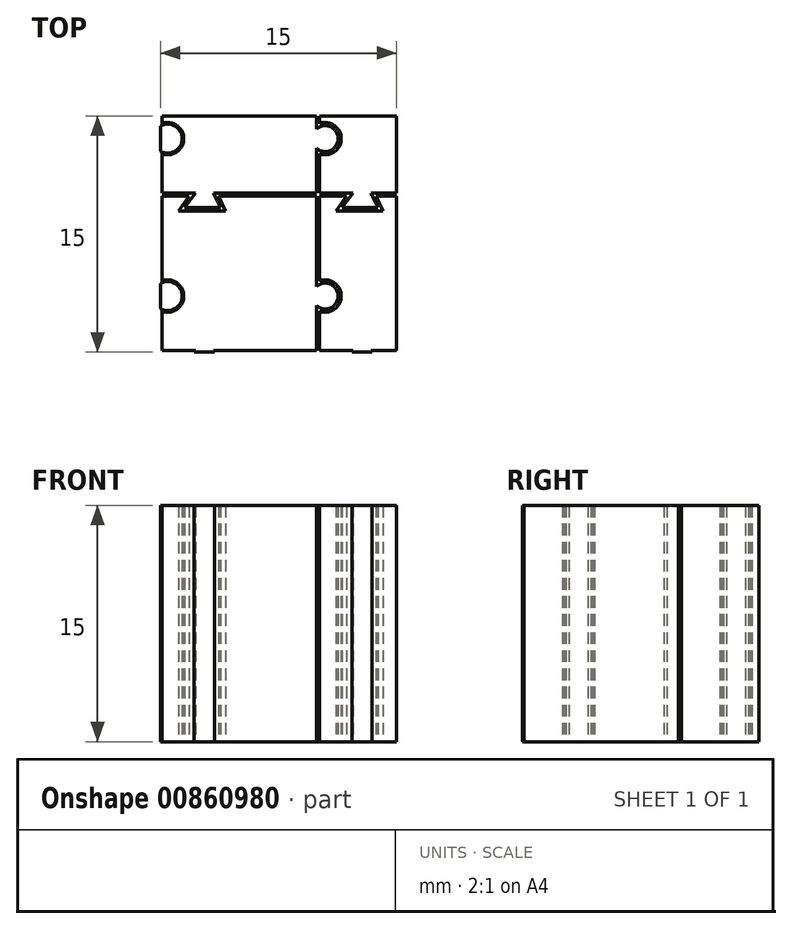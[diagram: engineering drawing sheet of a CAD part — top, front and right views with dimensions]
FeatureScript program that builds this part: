
annotation { "Feature Type Name" : "Feature", "Feature Type Description" : "" }
export const myFeature = defineFeature(function(context is Context, id is Id, definition is map)
    precondition{}
    {
        {
            var Q0;
            Q0=qCreatedBy(makeId("Top.planeOp"),FACE);
            var sketch = newSketch(context, id + "F0", { "sketchPlane" : qUnion([Q0])});
            skLineSegment(sketch, "E0.bottom", {"start": v(0, 0) * mm, "end": v(2.03, 0) * mm});
            skLineSegment(sketch, "E0.top", {"start": v(0, 10) * mm, "end": v(2.03, 10) * mm});
            skLineSegment(sketch, "E0.left", {"start": v(0, 0) * mm, "end": v(0, 2.75) * mm});
            skLineSegment(sketch, "E0.right", {"start": v(10, 0) * mm, "end": v(10, 2.75) * mm});
            skLineSegment(sketch, "E1", {"start": v(2.03, 10) * mm, "end": v(1.34, 9.07) * mm});
            skLineSegment(sketch, "E2", {"start": v(1.34, 9.07) * mm, "end": v(3.97, 9.07) * mm});
            skLineSegment(sketch, "E3", {"start": v(3.97, 9.07) * mm, "end": v(3.54, 10) * mm});
            skLineSegment(sketch, "E4.trimOffspring", {"start": v(3.54, 10) * mm, "end": v(10, 10) * mm});
            skLineSegment(sketch, "E5", {"start": v(2.03, 0) * mm, "end": v(1.34, -0.93) * mm});
            skLineSegment(sketch, "E6", {"start": v(1.34, -0.93) * mm, "end": v(3.97, -0.93) * mm});
            skLineSegment(sketch, "E7", {"start": v(3.97, -0.93) * mm, "end": v(3.54, 0) * mm});
            skLineSegment(sketch, "E8.trimOffspring", {"start": v(3.54, 0) * mm, "end": v(10, 0) * mm});
            skArc(sketch, "E9", {"start": v(0, 2.75) * mm, "mid": v(1.38, 3.55) * mm, "end": v(0, 4.36) * mm});
            skLineSegment(sketch, "E10.trimOffspring", {"start": v(0, 4.36) * mm, "end": v(0, 10) * mm});
            skArc(sketch, "E11", {"start": v(10, 2.75) * mm, "mid": v(11.38, 3.55) * mm, "end": v(10, 4.36) * mm});
            skLineSegment(sketch, "E12.trimOffspring", {"start": v(10, 4.36) * mm, "end": v(10, 10) * mm});
            skArc(sketch, "E13.0", {"start": v(0.1, 2.6) * mm, "mid": v(1.48, 3.55) * mm, "end": v(0.1, 4.51) * mm});
            skLineSegment(sketch, "E13.1", {"start": v(0.1, 0.1) * mm, "end": v(0.1, 2.6) * mm});
            skLineSegment(sketch, "E13.2", {"start": v(0.1, 0.1) * mm, "end": v(2.23, 0.1) * mm});
            skLineSegment(sketch, "E13.3", {"start": v(2.23, 0.1) * mm, "end": v(1.54, -0.83) * mm});
            skLineSegment(sketch, "E13.4", {"start": v(1.54, -0.83) * mm, "end": v(3.81, -0.83) * mm});
            skLineSegment(sketch, "E13.5", {"start": v(4.13, 8.97) * mm, "end": v(3.7, 9.9) * mm});
            skLineSegment(sketch, "E13.6", {"start": v(1.14, 8.97) * mm, "end": v(4.13, 8.97) * mm});
            skLineSegment(sketch, "E13.7", {"start": v(1.83, 9.9) * mm, "end": v(1.14, 8.97) * mm});
            skLineSegment(sketch, "E13.8", {"start": v(0.1, 9.9) * mm, "end": v(1.83, 9.9) * mm});
            skLineSegment(sketch, "E13.9", {"start": v(3.7, 9.9) * mm, "end": v(9.9, 9.9) * mm});
            skLineSegment(sketch, "E13.10", {"start": v(9.9, 4.16) * mm, "end": v(9.9, 9.9) * mm});
            skArc(sketch, "E13.11", {"start": v(9.9, 2.95) * mm, "mid": v(11.28, 3.55) * mm, "end": v(9.9, 4.16) * mm});
            skLineSegment(sketch, "E13.12", {"start": v(9.9, 0.1) * mm, "end": v(9.9, 2.95) * mm});
            skLineSegment(sketch, "E13.13", {"start": v(3.39, 0.1) * mm, "end": v(9.9, 0.1) * mm});
            skLineSegment(sketch, "E13.14", {"start": v(0.1, 4.51) * mm, "end": v(0.1, 9.9) * mm});
            skLineSegment(sketch, "E13.15", {"start": v(3.81, -0.83) * mm, "end": v(3.39, 0.1) * mm});
            skLineSegment(sketch, "E14.0.1.0", {"start": v(1.14, 18.97) * mm, "end": v(4.13, 18.97) * mm});
            skLineSegment(sketch, "E14.0.1.1", {"start": v(0.1, 19.9) * mm, "end": v(1.83, 19.9) * mm});
            skArc(sketch, "E14.0.1.3", {"start": v(10, 12.75) * mm, "mid": v(11.38, 13.55) * mm, "end": v(10, 14.36) * mm});
            skArc(sketch, "E14.0.1.4", {"start": v(9.9, 12.95) * mm, "mid": v(11.28, 13.55) * mm, "end": v(9.9, 14.16) * mm});
            skArc(sketch, "E14.0.1.5", {"start": v(0, 12.75) * mm, "mid": v(1.38, 13.55) * mm, "end": v(0, 14.36) * mm});
            skLineSegment(sketch, "E14.0.1.6", {"start": v(10, 10) * mm, "end": v(10, 12.75) * mm});
            skArc(sketch, "E14.0.1.7", {"start": v(0.1, 12.6) * mm, "mid": v(1.48, 13.55) * mm, "end": v(0.1, 14.51) * mm});
            skLineSegment(sketch, "E14.0.1.8", {"start": v(0.1, 10.1) * mm, "end": v(2.23, 10.1) * mm});
            skLineSegment(sketch, "E14.0.1.10", {"start": v(9.9, 10.1) * mm, "end": v(9.9, 12.95) * mm});
            skLineSegment(sketch, "E14.0.1.11", {"start": v(10, 14.36) * mm, "end": v(10, 20) * mm});
            skLineSegment(sketch, "E14.0.1.12", {"start": v(0, 20) * mm, "end": v(2.03, 20) * mm});
            skLineSegment(sketch, "E14.0.1.13", {"start": v(3.7, 19.9) * mm, "end": v(9.9, 19.9) * mm});
            skLineSegment(sketch, "E14.0.1.14", {"start": v(0, 14.36) * mm, "end": v(0, 20) * mm});
            skLineSegment(sketch, "E14.0.1.15", {"start": v(9.9, 14.16) * mm, "end": v(9.9, 19.9) * mm});
            skLineSegment(sketch, "E14.0.1.16", {"start": v(3.54, 20) * mm, "end": v(10, 20) * mm});
            skLineSegment(sketch, "E14.0.1.17", {"start": v(0.1, 10.1) * mm, "end": v(0.1, 12.6) * mm});
            skLineSegment(sketch, "E14.0.1.18", {"start": v(1.34, 19.07) * mm, "end": v(3.97, 19.07) * mm});
            skLineSegment(sketch, "E14.0.1.19", {"start": v(1.54, 9.17) * mm, "end": v(3.81, 9.17) * mm});
            skLineSegment(sketch, "E14.0.1.21", {"start": v(0.1, 14.51) * mm, "end": v(0.1, 19.9) * mm});
            skLineSegment(sketch, "E14.0.1.22", {"start": v(0, 10) * mm, "end": v(0, 12.75) * mm});
            skLineSegment(sketch, "E14.0.1.23", {"start": v(3.39, 10.1) * mm, "end": v(9.9, 10.1) * mm});
            skLineSegment(sketch, "E14.0.1.24", {"start": v(2.03, 20) * mm, "end": v(1.34, 19.07) * mm});
            skLineSegment(sketch, "E14.0.1.26", {"start": v(4.13, 18.97) * mm, "end": v(3.7, 19.9) * mm});
            skLineSegment(sketch, "E14.0.1.28", {"start": v(3.81, 9.17) * mm, "end": v(3.39, 10.1) * mm});
            skLineSegment(sketch, "E14.0.1.29", {"start": v(3.97, 19.07) * mm, "end": v(3.54, 20) * mm});
            skLineSegment(sketch, "E14.0.1.30", {"start": v(1.83, 19.9) * mm, "end": v(1.14, 18.97) * mm});
            skLineSegment(sketch, "E14.0.1.31", {"start": v(2.23, 10.1) * mm, "end": v(1.54, 9.17) * mm});
            skLineSegment(sketch, "E14.1.0.0", {"start": v(11.14, 8.97) * mm, "end": v(14.13, 8.97) * mm});
            skLineSegment(sketch, "E14.1.0.1", {"start": v(10.1, 9.9) * mm, "end": v(11.83, 9.9) * mm});
            skLineSegment(sketch, "E14.1.0.2", {"start": v(11.34, -0.93) * mm, "end": v(13.97, -0.93) * mm});
            skArc(sketch, "E14.1.0.3", {"start": v(20, 2.75) * mm, "mid": v(21.38, 3.55) * mm, "end": v(20, 4.36) * mm});
            skArc(sketch, "E14.1.0.4", {"start": v(19.9, 2.95) * mm, "mid": v(21.28, 3.55) * mm, "end": v(19.9, 4.16) * mm});
            skLineSegment(sketch, "E14.1.0.6", {"start": v(20, 0) * mm, "end": v(20, 2.75) * mm});
            skArc(sketch, "E14.1.0.7", {"start": v(10.1, 2.6) * mm, "mid": v(11.48, 3.55) * mm, "end": v(10.1, 4.51) * mm});
            skLineSegment(sketch, "E14.1.0.8", {"start": v(10.1, 0.1) * mm, "end": v(12.23, 0.1) * mm});
            skLineSegment(sketch, "E14.1.0.9", {"start": v(13.54, 0) * mm, "end": v(20, 0) * mm});
            skLineSegment(sketch, "E14.1.0.10", {"start": v(19.9, 0.1) * mm, "end": v(19.9, 2.95) * mm});
            skLineSegment(sketch, "E14.1.0.11", {"start": v(20, 4.36) * mm, "end": v(20, 10) * mm});
            skLineSegment(sketch, "E14.1.0.12", {"start": v(10, 10) * mm, "end": v(12.03, 10) * mm});
            skLineSegment(sketch, "E14.1.0.13", {"start": v(13.7, 9.9) * mm, "end": v(19.9, 9.9) * mm});
            skLineSegment(sketch, "E14.1.0.15", {"start": v(19.9, 4.16) * mm, "end": v(19.9, 9.9) * mm});
            skLineSegment(sketch, "E14.1.0.16", {"start": v(13.54, 10) * mm, "end": v(20, 10) * mm});
            skLineSegment(sketch, "E14.1.0.17", {"start": v(10.1, 0.1) * mm, "end": v(10.1, 2.6) * mm});
            skLineSegment(sketch, "E14.1.0.18", {"start": v(11.34, 9.07) * mm, "end": v(13.97, 9.07) * mm});
            skLineSegment(sketch, "E14.1.0.19", {"start": v(11.54, -0.83) * mm, "end": v(13.81, -0.83) * mm});
            skLineSegment(sketch, "E14.1.0.20", {"start": v(10, 0) * mm, "end": v(12.03, 0) * mm});
            skLineSegment(sketch, "E14.1.0.21", {"start": v(10.1, 4.51) * mm, "end": v(10.1, 9.9) * mm});
            skLineSegment(sketch, "E14.1.0.23", {"start": v(13.39, 0.1) * mm, "end": v(19.9, 0.1) * mm});
            skLineSegment(sketch, "E14.1.0.24", {"start": v(12.03, 10) * mm, "end": v(11.34, 9.07) * mm});
            skLineSegment(sketch, "E14.1.0.25", {"start": v(13.97, -0.93) * mm, "end": v(13.54, 0) * mm});
            skLineSegment(sketch, "E14.1.0.26", {"start": v(14.13, 8.97) * mm, "end": v(13.7, 9.9) * mm});
            skLineSegment(sketch, "E14.1.0.27", {"start": v(12.03, 0) * mm, "end": v(11.34, -0.93) * mm});
            skLineSegment(sketch, "E14.1.0.28", {"start": v(13.81, -0.83) * mm, "end": v(13.39, 0.1) * mm});
            skLineSegment(sketch, "E14.1.0.29", {"start": v(13.97, 9.07) * mm, "end": v(13.54, 10) * mm});
            skLineSegment(sketch, "E14.1.0.30", {"start": v(11.83, 9.9) * mm, "end": v(11.14, 8.97) * mm});
            skLineSegment(sketch, "E14.1.0.31", {"start": v(12.23, 0.1) * mm, "end": v(11.54, -0.83) * mm});
            skLineSegment(sketch, "E14.1.1.0", {"start": v(11.14, 18.97) * mm, "end": v(14.13, 18.97) * mm});
            skLineSegment(sketch, "E14.1.1.1", {"start": v(10.1, 19.9) * mm, "end": v(11.83, 19.9) * mm});
            skLineSegment(sketch, "E14.1.1.2", {"start": v(11.34, 9.07) * mm, "end": v(13.97, 9.07) * mm});
            skArc(sketch, "E14.1.1.3", {"start": v(20, 12.75) * mm, "mid": v(21.38, 13.55) * mm, "end": v(20, 14.36) * mm});
            skArc(sketch, "E14.1.1.4", {"start": v(19.9, 12.95) * mm, "mid": v(21.28, 13.55) * mm, "end": v(19.9, 14.16) * mm});
            skArc(sketch, "E14.1.1.5", {"start": v(10, 12.75) * mm, "mid": v(11.38, 13.55) * mm, "end": v(10, 14.36) * mm});
            skLineSegment(sketch, "E14.1.1.6", {"start": v(20, 10) * mm, "end": v(20, 12.75) * mm});
            skArc(sketch, "E14.1.1.7", {"start": v(10.1, 12.6) * mm, "mid": v(11.48, 13.55) * mm, "end": v(10.1, 14.51) * mm});
            skLineSegment(sketch, "E14.1.1.8", {"start": v(10.1, 10.1) * mm, "end": v(12.23, 10.1) * mm});
            skLineSegment(sketch, "E14.1.1.9", {"start": v(13.54, 10) * mm, "end": v(20, 10) * mm});
            skLineSegment(sketch, "E14.1.1.10", {"start": v(19.9, 10.1) * mm, "end": v(19.9, 12.95) * mm});
            skLineSegment(sketch, "E14.1.1.11", {"start": v(20, 14.36) * mm, "end": v(20, 20) * mm});
            skLineSegment(sketch, "E14.1.1.12", {"start": v(10, 20) * mm, "end": v(12.03, 20) * mm});
            skLineSegment(sketch, "E14.1.1.13", {"start": v(13.7, 19.9) * mm, "end": v(19.9, 19.9) * mm});
            skLineSegment(sketch, "E14.1.1.14", {"start": v(10, 14.36) * mm, "end": v(10, 20) * mm});
            skLineSegment(sketch, "E14.1.1.15", {"start": v(19.9, 14.16) * mm, "end": v(19.9, 19.9) * mm});
            skLineSegment(sketch, "E14.1.1.16", {"start": v(13.54, 20) * mm, "end": v(20, 20) * mm});
            skLineSegment(sketch, "E14.1.1.17", {"start": v(10.1, 10.1) * mm, "end": v(10.1, 12.6) * mm});
            skLineSegment(sketch, "E14.1.1.18", {"start": v(11.34, 19.07) * mm, "end": v(13.97, 19.07) * mm});
            skLineSegment(sketch, "E14.1.1.19", {"start": v(11.54, 9.17) * mm, "end": v(13.81, 9.17) * mm});
            skLineSegment(sketch, "E14.1.1.20", {"start": v(10, 10) * mm, "end": v(12.03, 10) * mm});
            skLineSegment(sketch, "E14.1.1.21", {"start": v(10.1, 14.51) * mm, "end": v(10.1, 19.9) * mm});
            skLineSegment(sketch, "E14.1.1.22", {"start": v(10, 10) * mm, "end": v(10, 12.75) * mm});
            skLineSegment(sketch, "E14.1.1.23", {"start": v(13.39, 10.1) * mm, "end": v(19.9, 10.1) * mm});
            skLineSegment(sketch, "E14.1.1.24", {"start": v(12.03, 20) * mm, "end": v(11.34, 19.07) * mm});
            skLineSegment(sketch, "E14.1.1.25", {"start": v(13.97, 9.07) * mm, "end": v(13.54, 10) * mm});
            skLineSegment(sketch, "E14.1.1.26", {"start": v(14.13, 18.97) * mm, "end": v(13.7, 19.9) * mm});
            skLineSegment(sketch, "E14.1.1.27", {"start": v(12.03, 10) * mm, "end": v(11.34, 9.07) * mm});
            skLineSegment(sketch, "E14.1.1.28", {"start": v(13.81, 9.17) * mm, "end": v(13.39, 10.1) * mm});
            skLineSegment(sketch, "E14.1.1.29", {"start": v(13.97, 19.07) * mm, "end": v(13.54, 20) * mm});
            skLineSegment(sketch, "E14.1.1.30", {"start": v(11.83, 19.9) * mm, "end": v(11.14, 18.97) * mm});
            skLineSegment(sketch, "E14.1.1.31", {"start": v(12.23, 10.1) * mm, "end": v(11.54, 9.17) * mm});
            skLineSegment(sketch, "E14.direction1", {"start": v(0, 0) * mm, "end": v(10, 0) * mm, "construction": true});
            skLineSegment(sketch, "E14.direction2", {"start": v(0, 0) * mm, "end": v(0, 10) * mm, "construction": true});
            skSolve(sketch);
        }
        {
            var Q0;
            Q0=qCreatedBy(makeId("Top.planeOp"),FACE);
            var sketch = newSketch(context, id + "F1", { "sketchPlane" : qUnion([Q0])});
            skLineSegment(sketch, "E15.bottom", {"start": v(0, 0) * mm, "end": v(15, 0) * mm});
            skLineSegment(sketch, "E15.top", {"start": v(0, 15) * mm, "end": v(15, 15) * mm});
            skLineSegment(sketch, "E15.left", {"start": v(0, 0) * mm, "end": v(0, 15) * mm});
            skLineSegment(sketch, "E15.right", {"start": v(15, 0) * mm, "end": v(15, 15) * mm});
            skSolve(sketch);
        }
        {
            var Q0;
            Q0=makeQuery(id+"F1.imprint","IMPRINT",FACE,{"disambiguationData":[TD([[makeQuery(id+"F1.imprint","IMPRINT",EDGE,{"derivedFrom":sQuery(id+"F1.wireOp",EDGE,"E15.bottom")}),1.0]])]});
            extrude(context, id + "F2", {"entities" : qUnion([Q0]), "depth" : 15 * mm, "offsetDistance" : 25 * mm});
        }
        {
            var Q0;
            Q0=makeQuery(id+"F0.imprint","IMPRINT",FACE,{"disambiguationData":[TD([[makeQuery(id+"F0.imprint","IMPRINT",EDGE,{"derivedFrom":sQuery(id+"F0.wireOp",EDGE,"E14.1.0.0")}),1.0]])]});
            var Q1;
            Q1=makeQuery(id+"F0.imprint","IMPRINT",FACE,{"disambiguationData":[TD([[makeQuery(id+"F0.imprint","IMPRINT",EDGE,{"derivedFrom":sQuery(id+"F0.wireOp",EDGE,"E14.0.1.0")}),1.0]])]});
            var Q2;
            Q2=makeQuery(id+"F0.imprint","IMPRINT",FACE,{"disambiguationData":[TD([[makeQuery(id+"F0.imprint","IMPRINT",EDGE,{"derivedFrom":sQuery(id+"F0.wireOp",EDGE,"E14.1.1.0")}),1.0]])]});
            var Q3;
            Q3=makeQuery(id+"F0.imprint","IMPRINT",FACE,{"disambiguationData":[TD([[makeQuery(id+"F0.imprint","IMPRINT",EDGE,{"derivedFrom":sQuery(id+"F0.wireOp",EDGE,"E0.bottom")}),1.0]])]});
            extrude(context, id + "F3", {"entities" : qUnion([Q0, Q1, Q2, Q3]), "operationType" : NewBodyOperationType.REMOVE, "endBound" : BoundingType.THROUGH_ALL, "depth" : 25 * mm, "offsetDistance" : 25 * mm});
        }
    });
